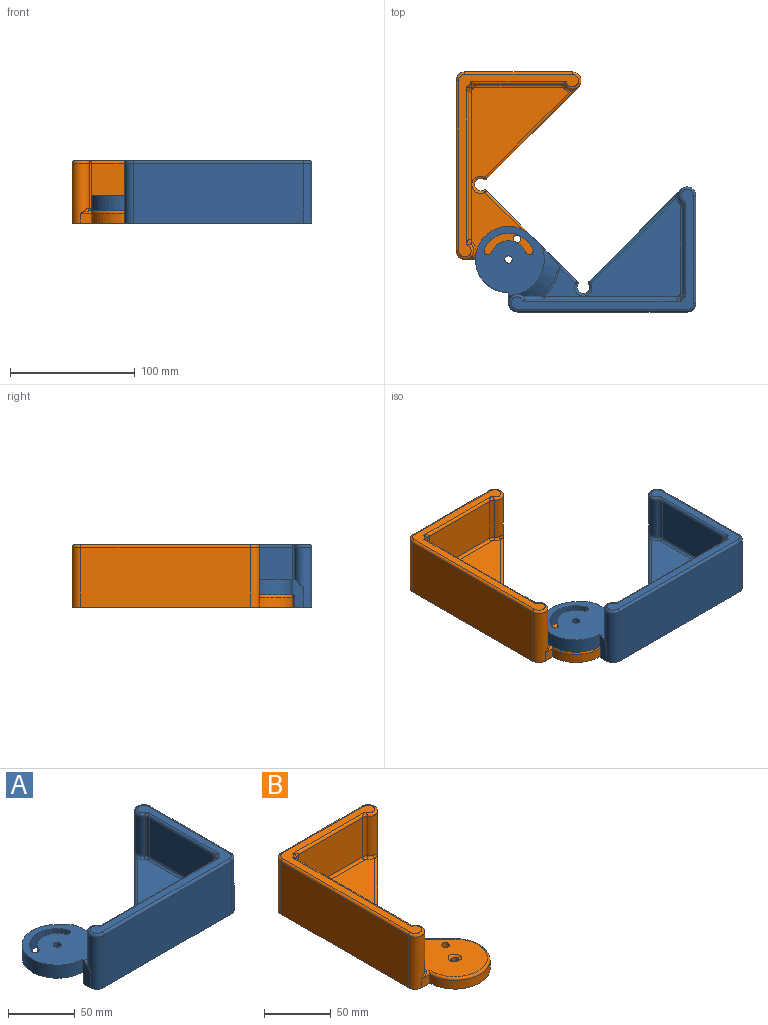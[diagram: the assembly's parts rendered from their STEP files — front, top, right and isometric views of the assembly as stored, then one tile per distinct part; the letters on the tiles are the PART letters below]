
ASSEMBLY  parts=2 mates=1
PART A: 59 faces, bbox 178.9x103.4x51.8 mm
  f0: plane 109.41x79.24mm, normal (0,0,1), area 3705mm2, adj f26,f27,f28,f29,f32,f34,f37,f39
  f1: plane 36.31x36.31mm, normal (0.71,0.71,0), area 617.8mm2, adj f2,f6,f16,f17,f23,f25,f36,f37
  f2: cylinder r=28mm len=40.39mm, axis (0,0,-1), area 568.1mm2, adj f1,f3,f6,f16
  f3: plane 22x8.49mm, normal (-1,0,0), area 151.4mm2, adj f2,f6,f10,f16,f17,f23,f30
  f4: plane 75.32x75.32mm, normal (-0.71,0.71,0), area 842.2mm2, adj f6,f8,f24,f31,f32
  f5: cylinder r=5mm len=10mm, axis (0,0,-1), area 165.3mm2, adj f6,f24,f25,f34
  f6: plane 150x100mm, normal (0,0,-1), area 7403.1mm2, adj f1,f2,f3,f4,f5,f8,f10,f11
  f7: plane 68.11x36mm, normal (-1,0,0), area 2452mm2, adj f28,f49,f54,f57
  f8: cylinder r=7mm len=48mm, axis (0,0,-1), area 1201.6mm2, adj f4,f6,f13,f29,f48,f57
  f9: cylinder r=7mm len=36mm, axis (0,0,-1), area 28.1mm2, adj f27,f47,f51,f54
  f10: cylinder r=7mm len=48mm, axis (0,0,-1), area 1052.5mm2, adj f3,f6,f11,f14,f30,f41,f43
  f11: plane 136x48mm, normal (0,-1,0), area 6528mm2, adj f6,f10,f12,f42
  f12: cylinder r=7mm len=48mm, axis (0,0,-1), area 527.8mm2, adj f6,f11,f13,f44
  f13: plane 86x48mm, normal (1,0,0), area 4128mm2, adj f6,f8,f12,f46
  f14: plane 120.73x36mm, normal (0,1,0), area 4275mm2, adj f10,f26,f41,f45,f51
  f15: plane 146x96mm, normal (0,0,1), area 1469.2mm2, adj f42,f43,f44,f45,f46,f47,f48,f49
  f16: plane 54.51x54.51mm, normal (0,0,-1), area 1984mm2, adj f1,f2,f3,f17,f18,f19,f20,f21
  f17: cylinder r=26.51mm len=53.03mm, axis (0,0,-1), area 1249.5mm2, adj f1,f3,f16,f23
  f18: cylinder r=21mm len=38.8mm, axis (0,0,-1), area 593.8mm2, adj f16,f19,f21,f23
  f19: cylinder r=3mm len=12mm, axis (0,0,-1), area 113.1mm2, adj f16,f18,f20,f23
  f20: cylinder r=15mm len=27.72mm, axis (0,0,-1), area 424.1mm2, adj f16,f19,f21,f23
  f21: cylinder r=3mm len=12mm, axis (0,0,-1), area 113.1mm2, adj f16,f18,f20,f23
  f22: cylinder r=3mm len=12mm, axis (0,0,-1), area 226.2mm2, adj f16,f23
  f23: plane 55.4x55.4mm, normal (0,0,1), area 2018.5mm2, adj f1,f3,f17,f18,f19,f20,f21,f22
  f24: cylinder r=2mm len=8mm, axis (0,0,-1), area 20.5mm2, adj f4,f5,f6,f33
  f25: cylinder r=2mm len=8mm, axis (0,0,-1), area 20.5mm2, adj f1,f5,f6,f35
  f26: cylinder r=2mm len=105.46mm, axis (-1,0,0), area 331.3mm2, adj f0,f14,f40,f52
  f27: torus R=9mm, axis (0,0,1), area 2.7mm2, adj f0,f9,f52,f55
  f28: cylinder r=2mm len=68.11mm, axis (0,-1,0), area 214mm2, adj f0,f7,f55,f58
  f29: torus R=9mm, axis (0,0,1), area 27mm2, adj f0,f8,f31,f58
  f30: cone r=28.62mm half-angle=45deg, axis (0,0,-1), area 651.7mm2, adj f3,f10,f23,f36,f39,f41
  f31: bspline ~7.12x5.78mm, area 8.3mm2, adj f4,f29,f32
  f32: cylinder r=2mm len=69.63mm, axis (0.71,0.71,0), area 303.1mm2, adj f0,f4,f31,f33
  f33: sphere r=2mm, area 5.1mm2, adj f24,f32,f34
  f34: torus R=7mm, axis (0,0,1), area 74.4mm2, adj f0,f5,f33,f35
  f35: sphere r=2mm, area 4mm2, adj f25,f34,f37
  f36: bspline ~20.22x19.34mm, area 46.8mm2, adj f1,f23,f30,f38
  f37: cylinder r=2mm len=14.09mm, axis (0.71,-0.71,0), area 56.3mm2, adj f0,f1,f35,f38
  f38: bspline ~4.72x3.33mm, area 8.2mm2, adj f1,f36,f37,f39
  f39: torus R=41.44mm, axis (0,0,1), area 43.7mm2, adj f0,f30,f38,f40
  f40: sphere r=2mm, area 3.3mm2, adj f26,f39,f41
  f41: bspline ~24.57x15.37mm, area 82.2mm2, adj f10,f14,f30,f40
  f42: cylinder r=2mm len=136mm, axis (-1,0,0), area 427.3mm2, adj f11,f15,f43,f44
  f43: torus R=5mm, axis (0,0,1), area 86.4mm2, adj f10,f15,f42,f45
  f44: torus R=5mm, axis (0,0,1), area 31mm2, adj f12,f15,f42,f46
  f45: cylinder r=2mm len=126.2mm, axis (1,0,0), area 387.9mm2, adj f14,f15,f43,f50
  f46: cylinder r=2mm len=86mm, axis (0,-1,0), area 270.2mm2, adj f13,f15,f44,f48
  f47: torus R=5mm, axis (0,0,1), area 7.2mm2, adj f9,f15,f50,f53
  f48: torus R=5mm, axis (0,0,1), area 83.4mm2, adj f8,f15,f46,f56
  f49: cylinder r=2mm len=76.2mm, axis (0,1,0), area 226.7mm2, adj f7,f15,f53,f56
  f50: bspline ~4.05x3.67mm, area 5.8mm2, adj f45,f47,f51
  f51: cylinder r=5mm len=36mm, axis (0,0,-1), area 151.4mm2, adj f9,f14,f50,f52
  f52: torus R=3mm, axis (0,0,1), area 11.3mm2, adj f0,f26,f27,f51
  f53: bspline ~4.05x3.67mm, area 5.8mm2, adj f47,f49,f54
  f54: cylinder r=5mm len=36mm, axis (0,0,-1), area 151.4mm2, adj f7,f9,f53,f55
  f55: torus R=3mm, axis (0,0,1), area 11.3mm2, adj f0,f27,f28,f54
  f56: bspline ~4.05x3.67mm, area 5.8mm2, adj f48,f49,f57
  f57: cylinder r=5mm len=36mm, axis (0,0,-1), area 151.4mm2, adj f7,f8,f56,f58
  f58: torus R=3mm, axis (0,0,1), area 11.3mm2, adj f0,f28,f29,f57
PART B: 69 faces, bbox 101.2x179.3x50 mm
  f0: plane 176.51x100mm, normal (0,0,-1), area 9525mm2, adj f2,f3,f4,f5,f6,f10,f11,f12
  f1: plane 162.51x79.24mm, normal (0,0,1), area 6130.9mm2, adj f19,f20,f21,f22,f23,f26,f27,f28
  f2: plane 8.49x8mm, normal (0,-1,0), area 67.9mm2, adj f0,f3,f14,f26
  f3: cylinder r=26.51mm len=53.03mm, axis (0,0,-1), area 833mm2, adj f0,f2,f4,f28
  f4: plane 36.31x36.31mm, normal (0.71,0.71,0), area 410.8mm2, adj f0,f3,f17,f30
  f5: cylinder r=5mm len=10mm, axis (0,0,-1), area 165.3mm2, adj f0,f17,f18,f31
  f6: plane 73.51x73.51mm, normal (0.71,-0.71,0), area 831.6mm2, adj f0,f10,f18,f27
  f7: cylinder r=3mm len=6mm, axis (0,0,-1), area 56.5mm2, adj f41,f68
  f8: plane 68.11x36mm, normal (0,-1,0), area 2452mm2, adj f21,f37,f49,f52
  f9: cylinder r=7mm len=36mm, axis (0,0,-1), area 28.1mm2, adj f19,f35,f43,f52
  f10: cylinder r=7mm len=48mm, axis (0,0,-1), area 1212mm2, adj f0,f6,f11,f23,f25,f39,f49
  f11: plane 86x48mm, normal (0,1,0), area 4128mm2, adj f0,f10,f12,f40
  f12: cylinder r=7mm len=48mm, axis (0,0,-1), area 527.8mm2, adj f0,f11,f13,f38
  f13: plane 136x48mm, normal (-1,0,0), area 6528mm2, adj f0,f12,f14,f36
  f14: cylinder r=7mm len=48mm, axis (0,0,-1), area 1146mm2, adj f0,f2,f13,f22,f24,f34,f46
  f15: plane 118.11x36mm, normal (1,0,0), area 4252mm2, adj f20,f33,f43,f46
  f16: plane 146x96mm, normal (0,0,1), area 1469.2mm2, adj f33,f34,f35,f36,f37,f38,f39,f40
  f17: cylinder r=2mm len=8mm, axis (0,0,-1), area 20.5mm2, adj f0,f4,f5,f32
  f18: cylinder r=2mm len=8mm, axis (0,0,-1), area 20.5mm2, adj f0,f5,f6,f29
  f19: torus R=9mm, axis (0,0,1), area 2.7mm2, adj f1,f9,f44,f53
  f20: cylinder r=2mm len=118.11mm, axis (0,1,0), area 371.1mm2, adj f1,f15,f44,f47
  f21: cylinder r=2mm len=68.11mm, axis (1,0,0), area 214mm2, adj f1,f8,f50,f53
  f22: torus R=9mm, axis (0,0,1), area 34.7mm2, adj f1,f14,f24,f47
  f23: torus R=9mm, axis (0,0,1), area 15.6mm2, adj f1,f10,f25,f50
  f24: bspline ~7.97x4mm, area 12mm2, adj f14,f22,f26
  f25: bspline ~7.34x4mm, area 12mm2, adj f10,f23,f27
  f26: cylinder r=2mm len=10.57mm, axis (-1,0,0), area 15.8mm2, adj f1,f2,f24,f28
  f27: cylinder r=2mm len=74.92mm, axis (-0.71,-0.71,0), area 313.4mm2, adj f1,f6,f25,f29
  f28: torus R=24.51mm, axis (0,0,1), area 320.4mm2, adj f1,f3,f26,f30
  f29: sphere r=2mm, area 5.1mm2, adj f18,f27,f31
  f30: cylinder r=2mm len=37.72mm, axis (0.71,-0.71,0), area 161.3mm2, adj f1,f4,f28,f32
  f31: torus R=7mm, axis (0,0,1), area 74.4mm2, adj f1,f5,f29,f32
  f32: sphere r=2mm, area 5.1mm2, adj f17,f30,f31
  f33: cylinder r=2mm len=126.2mm, axis (0,-1,0), area 379.3mm2, adj f15,f16,f42,f45
  f34: torus R=5mm, axis (0,0,1), area 81mm2, adj f14,f16,f36,f45
  f35: torus R=5mm, axis (0,0,1), area 7.2mm2, adj f9,f16,f42,f51
  f36: cylinder r=2mm len=136mm, axis (0,1,0), area 427.3mm2, adj f13,f16,f34,f38
  f37: cylinder r=2mm len=76.2mm, axis (-1,0,0), area 222.2mm2, adj f8,f16,f48,f51
  f38: torus R=5mm, axis (0,0,1), area 31mm2, adj f12,f16,f36,f40
  f39: torus R=5mm, axis (0,0,1), area 81mm2, adj f10,f16,f40,f48
  f40: cylinder r=2mm len=86mm, axis (1,0,0), area 270.2mm2, adj f11,f16,f38,f39
  f41: torus R=5mm, axis (0,0,1), area 73.6mm2, adj f1,f7
  f42: bspline ~4.05x3.67mm, area 10.3mm2, adj f33,f35,f43
  f43: cylinder r=5mm len=36mm, axis (0,0,-1), area 151.4mm2, adj f9,f15,f42,f44
  f44: torus R=3mm, axis (0,0,1), area 11.3mm2, adj f1,f19,f20,f43
  f45: bspline ~4.05x3.67mm, area 10.3mm2, adj f33,f34,f46
  f46: cylinder r=5mm len=36mm, axis (0,0,-1), area 151.4mm2, adj f14,f15,f45,f47
  f47: torus R=3mm, axis (0,0,1), area 11.3mm2, adj f1,f20,f22,f46
  f48: bspline ~4.05x3.67mm, area 10.3mm2, adj f37,f39,f49
  f49: cylinder r=5mm len=36mm, axis (0,0,-1), area 151.4mm2, adj f8,f10,f48,f50
  f50: torus R=3mm, axis (0,0,1), area 11.3mm2, adj f1,f21,f23,f49
  f51: bspline ~4.05x3.67mm, area 10.3mm2, adj f35,f37,f52
  f52: cylinder r=5mm len=36mm, axis (0,0,-1), area 151.4mm2, adj f8,f9,f51,f53
  f53: torus R=3mm, axis (0,0,1), area 11.3mm2, adj f1,f19,f21,f52
  f54: cylinder r=3mm len=6mm, axis (0,0,1), area 94.2mm2, adj f1,f61
  f55: plane 5x5mm, normal (0.87,0.5,0), area 28.9mm2, adj f0,f56,f60,f61
  f56: plane 5.77x5mm, normal (0,1,0), area 28.9mm2, adj f0,f55,f57,f61
  f57: plane 5x5mm, normal (-0.87,0.5,0), area 28.9mm2, adj f0,f56,f58,f61
  f58: plane 5x5mm, normal (-0.87,-0.5,0), area 28.9mm2, adj f0,f57,f59,f61
  f59: plane 5.77x5mm, normal (0,-1,0), area 28.9mm2, adj f0,f58,f60,f61
  f60: plane 5x5mm, normal (0.87,-0.5,0), area 28.9mm2, adj f0,f55,f59,f61
  f61: plane 11.55x10mm, normal (0,0,-1), area 58.3mm2, adj f54,f55,f56,f57,f58,f59,f60
  f62: plane 5.77x5mm, normal (0,-1,0), area 28.9mm2, adj f0,f63,f67,f68
  f63: plane 5x5mm, normal (0.87,-0.5,0), area 28.9mm2, adj f0,f62,f64,f68
  f64: plane 5x5mm, normal (0.87,0.5,0), area 28.9mm2, adj f0,f63,f65,f68
  f65: plane 5.77x5mm, normal (0,1,0), area 28.9mm2, adj f0,f64,f66,f68
  f66: plane 5x5mm, normal (-0.87,0.5,0), area 28.9mm2, adj f0,f65,f67,f68
  f67: plane 5x5mm, normal (-0.87,-0.5,0), area 28.9mm2, adj f0,f62,f66,f68
  f68: plane 11.55x10mm, normal (0,0,-1), area 58.3mm2, adj f7,f62,f63,f64,f65,f66,f67
PLACE A t=(68.76,46.07,-6.76)mm
PLACE B t=(68.76,46.07,-6.76)mm
MATE revolute B.f3 <-> A.f2  axis (0,0,1) through (10.76,46.07,3.24)mm
